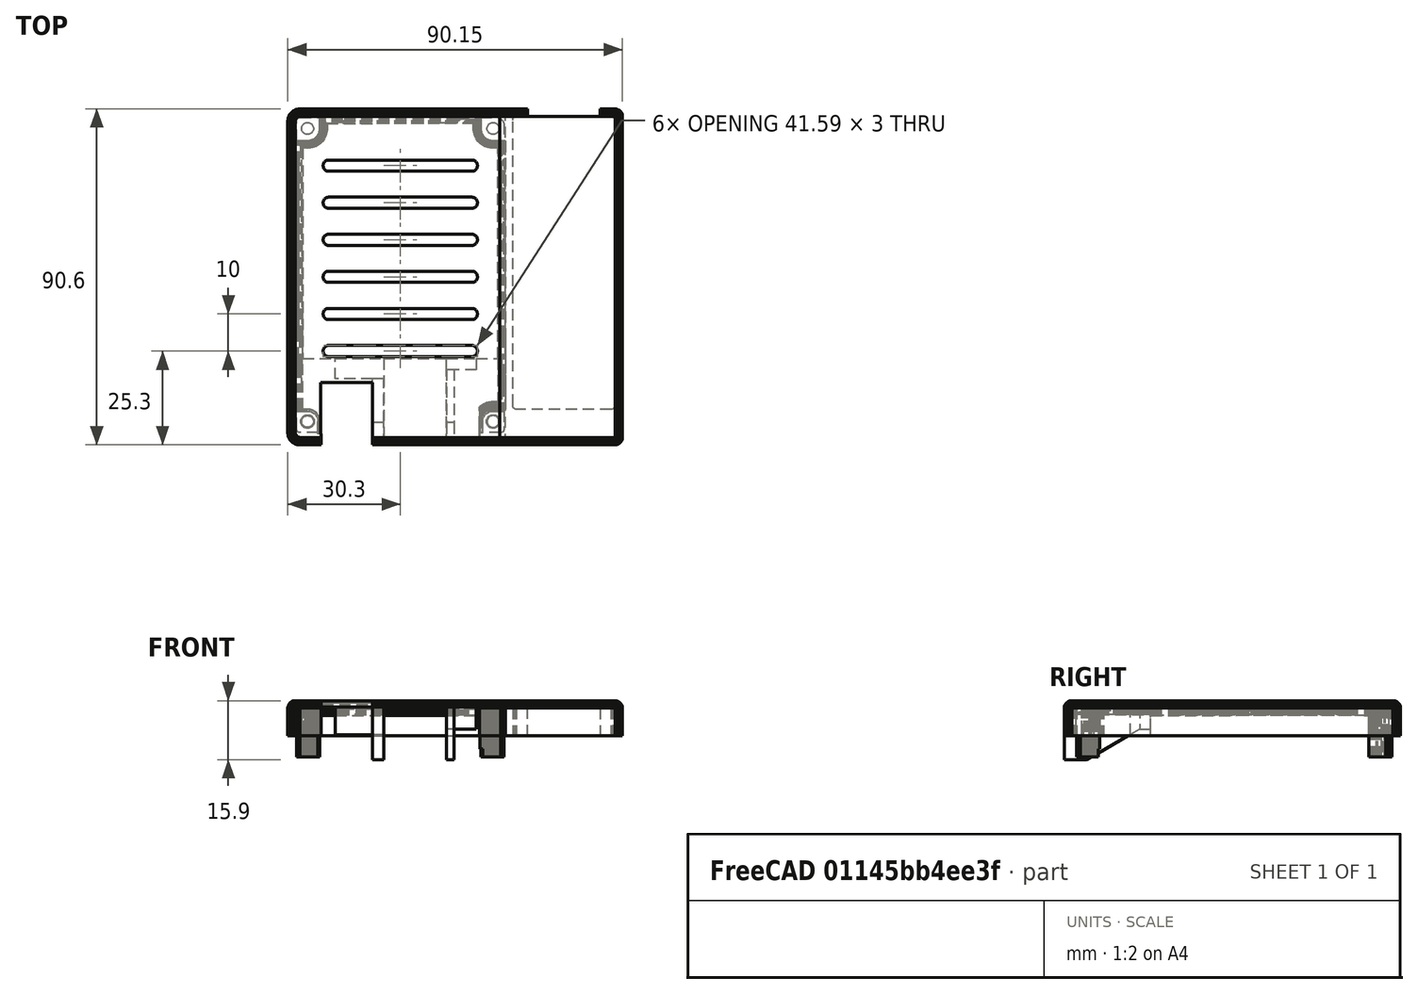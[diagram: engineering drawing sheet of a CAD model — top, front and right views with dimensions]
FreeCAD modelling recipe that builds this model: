
FCSTD DOCUMENT  (FreeCAD 1.0R38806 (Git))
Label: Top_Combined
License: All rights reserved
LicenseURL: https://en.wikipedia.org/wiki/All_rights_reserved
objects: Part::Feature×2, PartDesign::FeatureBase×2, PartDesign::Body×2, PartDesign::Boolean×1
note: 10 computed .brp shape members not serialized (recipe doc carries the construction recipe); baked Part::Feature solids carry a one-line shape summary decoded from their .brp

FEATURE [Part::Feature] Orange_PI_PC_Case_Top001_solid  label="Orange_PI_PC_Case_Top"
  Placement = pos=(0,3.9e-15,-17.5) rot=(1,0,0;1.5708rad)
  shape: bbox 60.6 x 90.6 x 15.9 mm, 8178 faces (baked)
FEATURE [PartDesign::FeatureBase] BaseFeature  label="Top_Case_Base"
  BaseFeature = -> Orange_PI_PC_Case_Top001_solid
  Placement = pos=(0,0,-17.5) rot=(1,0,0;1.5708rad)
  Suppressed = false
FEATURE [Part::Feature] Top_Extension_Model001_solid  label="Top_Extension_Model"
  shape: bbox 33 x 90.6 x 9.5 mm, 396 faces (baked)
FEATURE [PartDesign::FeatureBase] BaseFeature001  label="Top_Extension_Base"
  BaseFeature = -> Top_Extension_Model001_solid
  Suppressed = false
FEATURE [PartDesign::Body] Body001  label="Top_Extension"
  AllowCompound = false
  BaseFeature = -> Top_Extension_Model001_solid
  Group = -> [BaseFeature001]
  Origin = -> Origin001
  Tip = -> BaseFeature001
FEATURE [PartDesign::Boolean] Boolean
  BaseFeature = -> BaseFeature
  Group = -> [Top_Extension_Model001_solid,Body001]
  Refine = true
  Suppressed = false
  Type = 0
  UsePlacement = true
FEATURE [PartDesign::Body] Body  label="Top_Case"
  AllowCompound = false
  BaseFeature = -> Orange_PI_PC_Case_Top001_solid
  Group = -> [BaseFeature,Boolean]
  Origin = -> Origin
  Tip = -> Boolean
